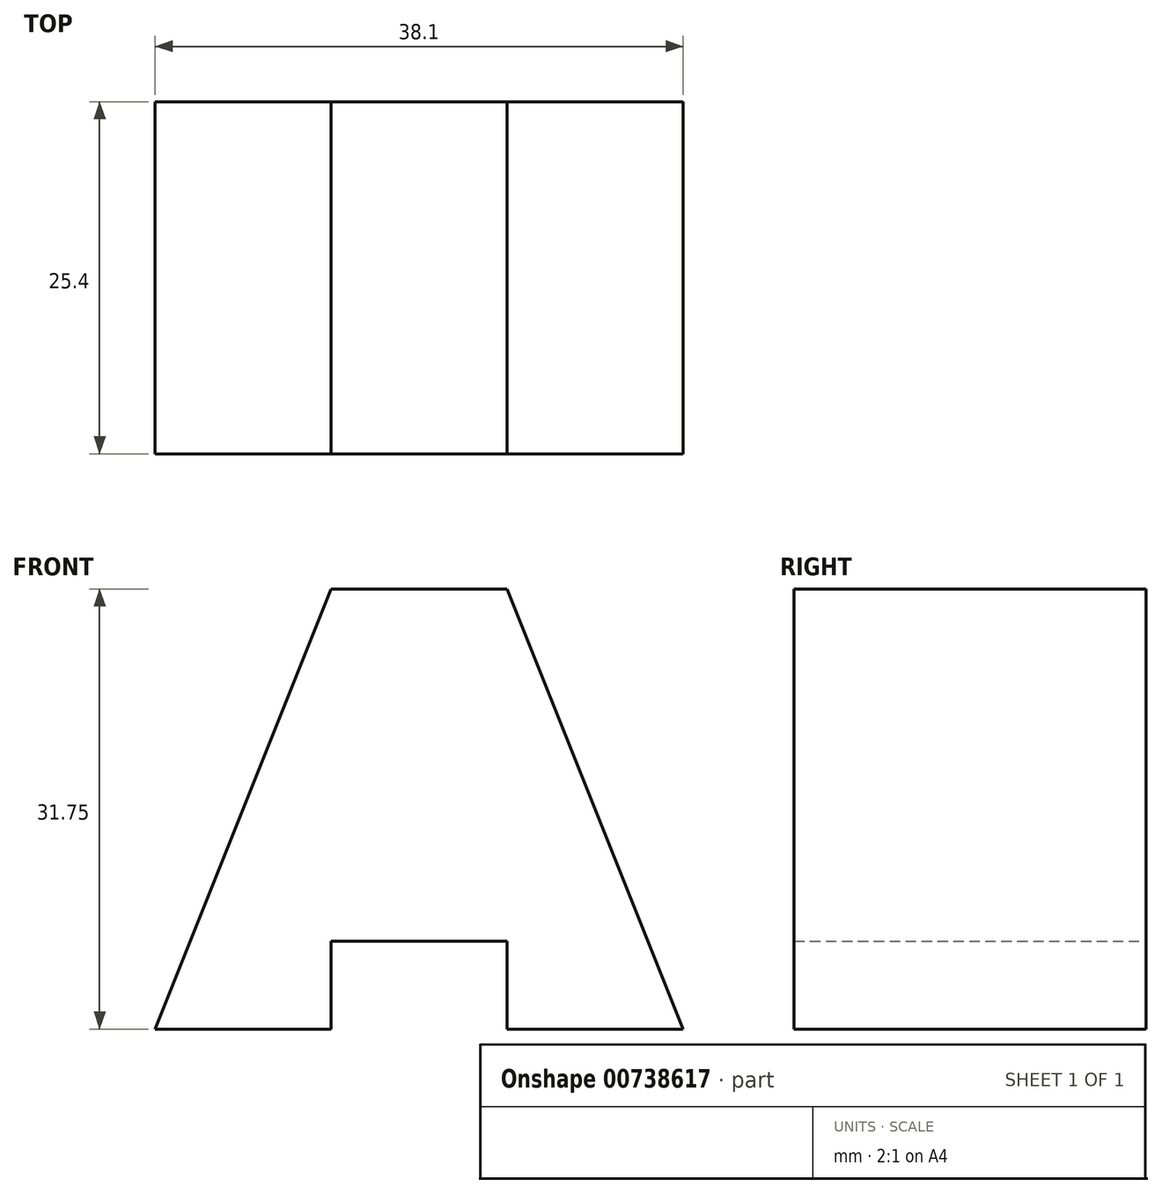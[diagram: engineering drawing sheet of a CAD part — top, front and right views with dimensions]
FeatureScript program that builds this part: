
annotation { "Feature Type Name" : "Feature", "Feature Type Description" : "" }
export const myFeature = defineFeature(function(context is Context, id is Id, definition is map)
    precondition{}
    {
        {
            var Q0;
            Q0=qCreatedBy(makeId("Front.planeOp"),FACE);
            var sketch = newSketch(context, id + "F0", { "sketchPlane" : qUnion([Q0])});
            skLineSegment(sketch, "E0.bottom", {"start": v(0, 0) * mm, "end": v(38.1, 0) * mm});
            skLineSegment(sketch, "E0.top", {"start": v(0, 31.75) * mm, "end": v(38.1, 31.75) * mm});
            skLineSegment(sketch, "E0.left", {"start": v(0, 0) * mm, "end": v(0, 31.75) * mm});
            skLineSegment(sketch, "E0.right", {"start": v(38.1, 0) * mm, "end": v(38.1, 31.75) * mm});
            skLineSegment(sketch, "E1", {"start": v(0, 0) * mm, "end": v(12.7, 0) * mm});
            skLineSegment(sketch, "E2", {"start": v(12.7, 0) * mm, "end": v(12.7, 6.35) * mm});
            skLineSegment(sketch, "E3", {"start": v(12.7, 6.35) * mm, "end": v(25.4, 6.35) * mm});
            skLineSegment(sketch, "E4", {"start": v(25.4, 6.35) * mm, "end": v(25.4, 0) * mm});
            skLineSegment(sketch, "E5", {"start": v(0, 31.75) * mm, "end": v(12.7, 31.75) * mm});
            skLineSegment(sketch, "E6", {"start": v(12.7, 31.75) * mm, "end": v(0, 0) * mm});
            skLineSegment(sketch, "E7", {"start": v(12.7, 31.75) * mm, "end": v(25.4, 31.75) * mm});
            skLineSegment(sketch, "E8", {"start": v(25.4, 31.75) * mm, "end": v(38.1, 0) * mm});
            skSolve(sketch);
        }
        {
            var Q0;
            {var subQ0=sQuery(id+"F0.wireOp",EDGE,"E2");Q0=makeQuery(id+"F0.imprint","IMPRINT",FACE,{"disambiguationData":[TD([[makeQuery(id+"F0.imprint","IMPRINT",EDGE,{"derivedFrom":subQ0}),1.0]])]});}
            extrude(context, id + "F1", {"entities" : qUnion([Q0]), "depth" : 25.4 * mm, "offsetDistance" : 25.4 * mm});
        }
    });
